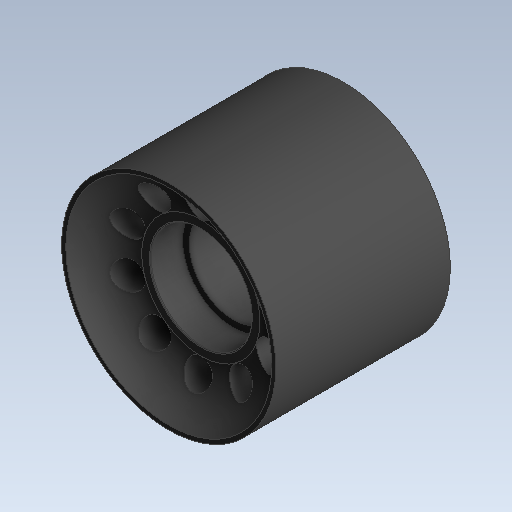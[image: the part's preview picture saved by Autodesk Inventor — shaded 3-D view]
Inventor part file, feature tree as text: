
AUTODESK INVENTOR PART (.ipt)
format: ipt  version: 2020.1 (Build 241239000, 239)  size: 344,576 bytes
history: native  units: mm
features: sketch x5, extrude x4, mirror x2, fillet x2, revolve x1, pattern_circular x1, plane x1
ambient origin geometry x8: Origin, YZ Plane, XZ Plane, XY Plane, X Axis, Y Axis, Z Axis, Center Point
bodies: Solid1 (feature_tree)
feature tree (16):
  extrude  "Extrusion1"  Depth=19.0mm
  extrude  "Extrusion2"  Depth=31.7mm
  revolve  "Revolution1"  [1 undecoded]
  mirror  "Mirror2"
  fillet  "Fillet1"  Radius=100.0mm
  extrude  "Extrusion4"  Depth=30.0mm
  pattern_circular  "Circular Pattern1"  [2 undecoded]
  plane  "Work Plane1"
  extrude  "Extrusion5"  Depth=0.2mm
  mirror  "Mirror3"
  fillet  "Fillet5"  Radius=12.0mm
  sketch  "Sketch1"  dims[d0=38.0mm d1=0.0mm d2=19.0mm]
  sketch  "Sketch2"  dims[d3=56.0mm d4=0.0mm d8=31.7mm]
  sketch  "Sketch4"  dims[d9=5.8mm d10=60.75mm d11=0.0mm d12=100.0mm d13=360.0deg]
  sketch  "Sketch5"  dims[d15=46.6mm d18=30.0mm]
  sketch  "Sketch7"  dims[d19=90.0deg d20=10.0mm d31=44.8mm d32=12.0mm d33=5.0mm d34=22.0mm d35=20.0mm d36=0.0mm d37=0.2mm]
note: 3 required parameter values undecoded (feature->parameter linkage not recoverable at this tier; creation-order binding heuristic only, values carry confidence <= 0.55)